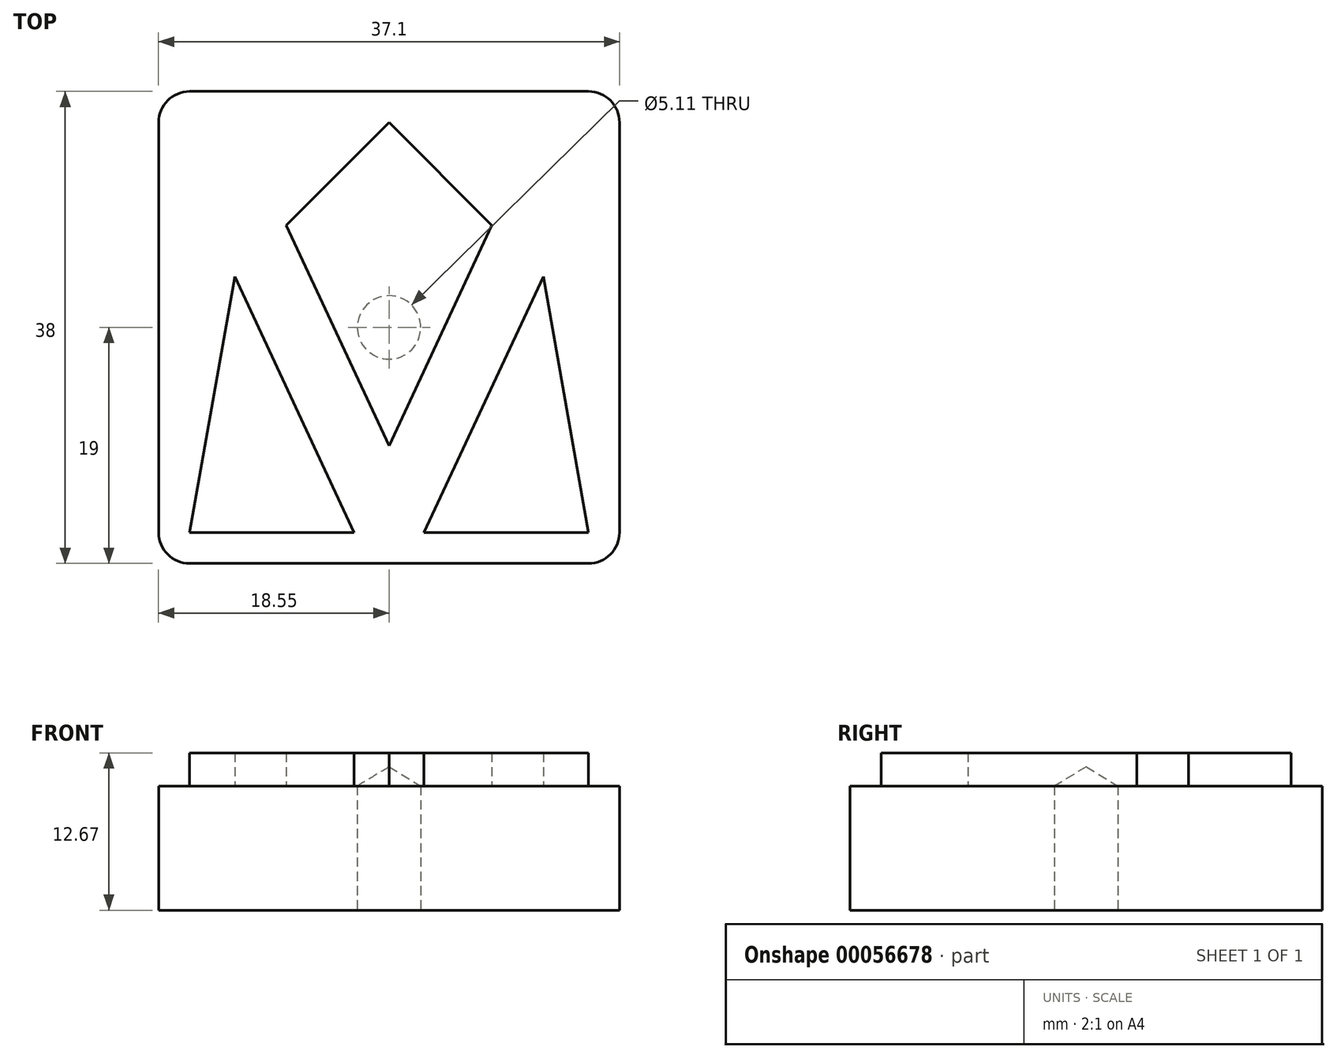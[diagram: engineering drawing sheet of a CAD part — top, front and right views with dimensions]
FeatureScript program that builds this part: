
annotation { "Feature Type Name" : "Feature", "Feature Type Description" : "" }
export const myFeature = defineFeature(function(context is Context, id is Id, definition is map)
    precondition{}
    {
        {
            var Q0;
            Q0=qCreatedBy(makeId("Top.planeOp"),FACE);
            var sketch = newSketch(context, id + "F0", { "sketchPlane" : qUnion([Q0])});
            skLineSegment(sketch, "E0", {"start": v(0, 33) * mm, "end": v(-33, 0) * mm});
            skLineSegment(sketch, "E1", {"start": v(-8.28, 24.72) * mm, "end": v(0, 6.97) * mm});
            skLineSegment(sketch, "E2", {"start": v(0, 33) * mm, "end": v(0, 0) * mm, "construction": true});
            skLineSegment(sketch, "E3", {"start": v(-12.42, 20.58) * mm, "end": v(-2.82, 0) * mm});
            skLineSegment(sketch, "E4", {"start": v(-12.42, 20.58) * mm, "end": v(-16.05, 0) * mm});
            skLineSegment(sketch, "E5", {"start": v(-33, 0) * mm, "end": v(0, 0) * mm});
            skLineSegment(sketch, "E6.MirrorCS", {"start": v(33, 0) * mm, "end": v(0, 0) * mm});
            skLineSegment(sketch, "E7.MirrorCS", {"start": v(12.42, 20.58) * mm, "end": v(16.05, 0) * mm});
            skLineSegment(sketch, "E8.MirrorCS", {"start": v(12.42, 20.58) * mm, "end": v(2.82, 0) * mm});
            skLineSegment(sketch, "E9.MirrorCS", {"start": v(0, 33) * mm, "end": v(33, 0) * mm});
            skLineSegment(sketch, "E10.MirrorCS", {"start": v(8.28, 24.72) * mm, "end": v(0, 6.97) * mm});
            skLineSegment(sketch, "E11.bottom", {"start": v(-18.55, 35.5) * mm, "end": v(18.55, 35.5) * mm});
            skLineSegment(sketch, "E11.top", {"start": v(-18.55, -2.5) * mm, "end": v(18.55, -2.5) * mm});
            skLineSegment(sketch, "E12", {"start": v(-18.55, 35.5) * mm, "end": v(-18.55, -2.5) * mm});
            skLineSegment(sketch, "E13", {"start": v(18.55, 35.5) * mm, "end": v(18.55, -2.5) * mm});
            skPoint(sketch, "E14.orphan", {"position": v(-33, 35.5) * mm});
            skPoint(sketch, "E15.orphan", {"position": v(33, -2.5) * mm});
            skSolve(sketch);
        }
        {
            var Q0;
            {var subQ4=sQuery(id+"F0.wireOp",EDGE,"E11.bottom");Q0=makeQuery(id+"F0.imprint","IMPRINT",FACE,{"disambiguationData":[TD([[makeQuery(id+"F0.imprint","IMPRINT",EDGE,{"derivedFrom":subQ4}),-1.0]])]});}
            var Q1;
            {var subQ4=sQuery(id+"F0.wireOp",EDGE,"E11.top");Q1=makeQuery(id+"F0.imprint","IMPRINT",FACE,{"disambiguationData":[TD([[makeQuery(id+"F0.imprint","IMPRINT",EDGE,{"derivedFrom":subQ4}),1.0]])]});}
            var Q2;
            {var subQ3=sQuery(id+"F0.wireOp",EDGE,"E4");Q2=makeQuery(id+"F0.imprint","IMPRINT",FACE,{"disambiguationData":[TD([[makeQuery(id+"F0.imprint","IMPRINT",EDGE,{"derivedFrom":subQ3}),-1.0]])]});}
            var Q3;
            {var subQ0=sQuery(id+"F0.wireOp",EDGE,"E3");Q3=makeQuery(id+"F0.imprint","IMPRINT",FACE,{"disambiguationData":[TD([[makeQuery(id+"F0.imprint","IMPRINT",EDGE,{"derivedFrom":subQ0}),-1.0]])]});}
            var Q4;
            {var subQ4=sQuery(id+"F0.wireOp",EDGE,"E1");Q4=makeQuery(id+"F0.imprint","IMPRINT",FACE,{"disambiguationData":[TD([[makeQuery(id+"F0.imprint","IMPRINT",EDGE,{"derivedFrom":subQ4}),-1.0]])]});}
            var Q5;
            {var subQ0=sQuery(id+"F0.wireOp",EDGE,"E7.MirrorCS");Q5=makeQuery(id+"F0.imprint","IMPRINT",FACE,{"disambiguationData":[TD([[makeQuery(id+"F0.imprint","IMPRINT",EDGE,{"derivedFrom":subQ0}),-1.0]])]});}
            var Q6;
            {var subQ3=sQuery(id+"F0.wireOp",EDGE,"E7.MirrorCS");Q6=makeQuery(id+"F0.imprint","IMPRINT",FACE,{"disambiguationData":[TD([[makeQuery(id+"F0.imprint","IMPRINT",EDGE,{"derivedFrom":subQ3}),1.0]])]});}
            var Q7;
            {var subQ3=sQuery(id+"F0.wireOp",EDGE,"E1");Q7=makeQuery(id+"F0.imprint","IMPRINT",FACE,{"disambiguationData":[TD([[makeQuery(id+"F0.imprint","IMPRINT",EDGE,{"derivedFrom":subQ3}),1.0]])]});}
            extrude(context, id + "F1", {"entities" : qUnion([Q0, Q1, Q2, Q3, Q4, Q5, Q6, Q7]), "depth" : 10 * mm});
        }
        {
            var Q0;
            {var subQ0=sQuery(id+"F0.wireOp",EDGE,"E7.MirrorCS");Q0=makeQuery(id+"F0.imprint","IMPRINT",FACE,{"disambiguationData":[TD([[makeQuery(id+"F0.imprint","IMPRINT",EDGE,{"derivedFrom":subQ0}),-1.0]])]});}
            var Q1;
            {var subQ3=sQuery(id+"F0.wireOp",EDGE,"E1");Q1=makeQuery(id+"F0.imprint","IMPRINT",FACE,{"disambiguationData":[TD([[makeQuery(id+"F0.imprint","IMPRINT",EDGE,{"derivedFrom":subQ3}),1.0]])]});}
            var Q2;
            {var subQ0=sQuery(id+"F0.wireOp",EDGE,"E3");Q2=makeQuery(id+"F0.imprint","IMPRINT",FACE,{"disambiguationData":[TD([[makeQuery(id+"F0.imprint","IMPRINT",EDGE,{"derivedFrom":subQ0}),-1.0]])]});}
            extrude(context, id + "F2", {"entities" : qUnion([Q0, Q1, Q2]), "operationType" : NewBodyOperationType.ADD, "depth" : 12.67 * mm});
        }
        {
            var Q0;
            Q0=makeQuery(id+"F1.opExtrude","CAP_FACE",FACE,{"disambiguationData":[OSD([sQuery(id+"F0.wireOp",EDGE,"E11.bottom"),sQuery(id+"F0.wireOp",EDGE,"E11.top"),sQuery(id+"F0.wireOp",EDGE,"E11.left"),sQuery(id+"F0.wireOp",EDGE,"E11.right")])],"isStart":true});
            var sketch = newSketch(context, id + "F3", { "sketchPlane" : qUnion([Q0])});
            skPoint(sketch, "E16", {"position": v(0, -16.5) * mm});
            skPoint(sketch, "E16.positionSnap0", {"position": v(-18.55, -16.5) * mm});
            skPoint(sketch, "E16.positionSnap1", {"position": v(0, 2.5) * mm});
            skSolve(sketch);
        }
        {
            var Q0;
            Q0=sQuery(id+"F3.wireOp",VERTEX,"E16");
            var Q1;
            Q1=makeQuery(id+"F1.opExtrude","SWEPT_BODY",BODY,{"disambiguationData":[OSD([sQuery(id+"F0.wireOp",EDGE,"E11.bottom"),sQuery(id+"F0.wireOp",EDGE,"E11.top"),sQuery(id+"F0.wireOp",EDGE,"E11.left"),sQuery(id+"F0.wireOp",EDGE,"E11.right")])]});
            hole(context, id + "F4", {"style" : HoleStyle.SIMPLE, "endStyle" : HoleEndStyle.BLIND, "standardTappedOrClearance" : lookupTablePath({ "standard" : "ANSI", "engagement" : "75%", "pitch" : "20 tpi", "size" : "1/4", "type" : "Tapped" }), "standardBlindInLast" : lookupTablePath({ "standard" : "ANSI", "engagement" : "75%", "pitch" : "20 tpi", "size" : "1/4", "type" : "Tapped" }), "holeDiameter" : 5.1 * mm, "holeDepth" : 10 * mm, "locations" : qUnion([Q0]), "scope" : qUnion([Q1]), "majorDiameter" : 6.35 * mm});
        }
        {
            var Q0;
            Q0=makeQuery(id+"F1.opExtrude","SWEPT_EDGE",EDGE,{"disambiguationData":[OSD([sQuery(id+"F0.wireOp",EDGE,"E11.bottom"),sQuery(id+"F0.wireOp",EDGE,"E12")])]});
            var Q1;
            Q1=makeQuery(id+"F1.opExtrude","SWEPT_EDGE",EDGE,{"disambiguationData":[OSD([sQuery(id+"F0.wireOp",EDGE,"E11.bottom"),sQuery(id+"F0.wireOp",EDGE,"E13")])]});
            var Q2;
            Q2=makeQuery(id+"F1.opExtrude","SWEPT_EDGE",EDGE,{"disambiguationData":[OSD([sQuery(id+"F0.wireOp",EDGE,"E11.top"),sQuery(id+"F0.wireOp",EDGE,"E13")])]});
            var Q3;
            Q3=makeQuery(id+"F1.opExtrude","SWEPT_EDGE",EDGE,{"disambiguationData":[OSD([sQuery(id+"F0.wireOp",EDGE,"E11.top"),sQuery(id+"F0.wireOp",EDGE,"E12")])]});
            fillet(context, id + "F5", {"entities" : qUnion([Q0, Q1, Q2, Q3]), "radius" : 2.5 * mm, "tangentPropagation" : true, "allowEdgeOverflow" : false});
        }
    });
